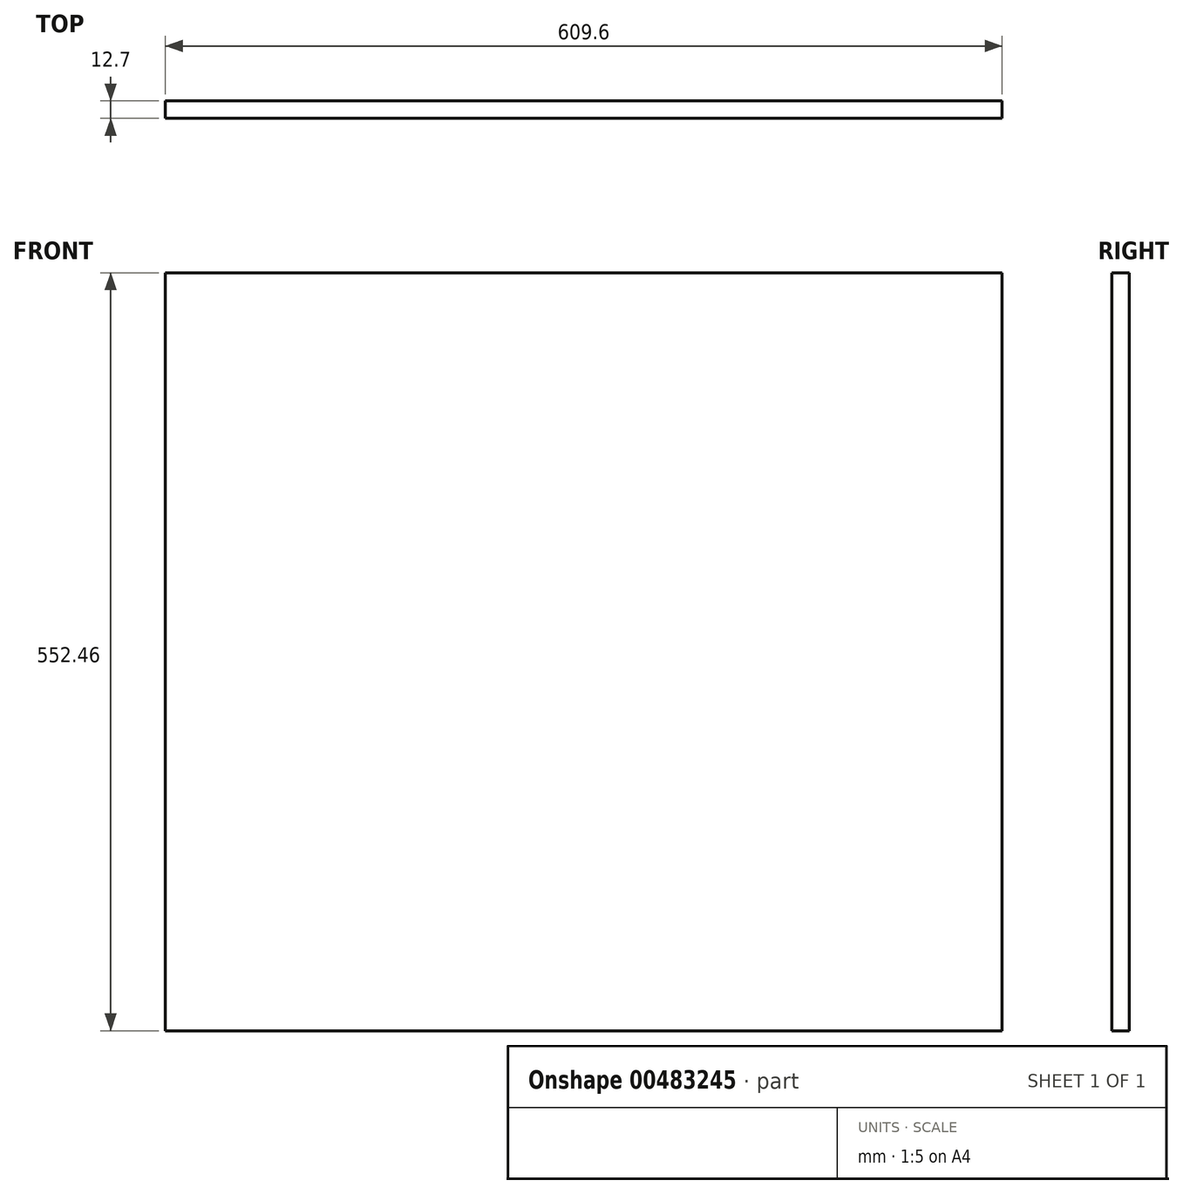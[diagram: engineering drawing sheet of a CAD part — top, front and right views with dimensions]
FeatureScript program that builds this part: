
annotation { "Feature Type Name" : "Feature", "Feature Type Description" : "" }
export const myFeature = defineFeature(function(context is Context, id is Id, definition is map)
    precondition{}
    {
        {
            var Q0;
            Q0=qCreatedBy(makeId("Front.planeOp"),FACE);
            var sketch = newSketch(context, id + "F0", { "sketchPlane" : qUnion([Q0])});
            skLineSegment(sketch, "E0.bottom", {"start": v(304.8, 276.23) * mm, "end": v(-304.8, 276.23) * mm});
            skLineSegment(sketch, "E0.top", {"start": v(304.8, -276.23) * mm, "end": v(-304.8, -276.23) * mm});
            skLineSegment(sketch, "E0.left", {"start": v(304.8, 276.23) * mm, "end": v(304.8, -276.23) * mm});
            skLineSegment(sketch, "E0.right", {"start": v(-304.8, 276.23) * mm, "end": v(-304.8, -276.23) * mm});
            skPoint(sketch, "E0.middle", {"position": v(0, 0) * mm});
            skSolve(sketch);
        }
        {
            var Q0;
            Q0 = qSketchRegion(id + "F0", true);
            extrude(context, id + "F1", {"entities" : qUnion([Q0]), "depth" : 12.7 * mm});
        }
    });
